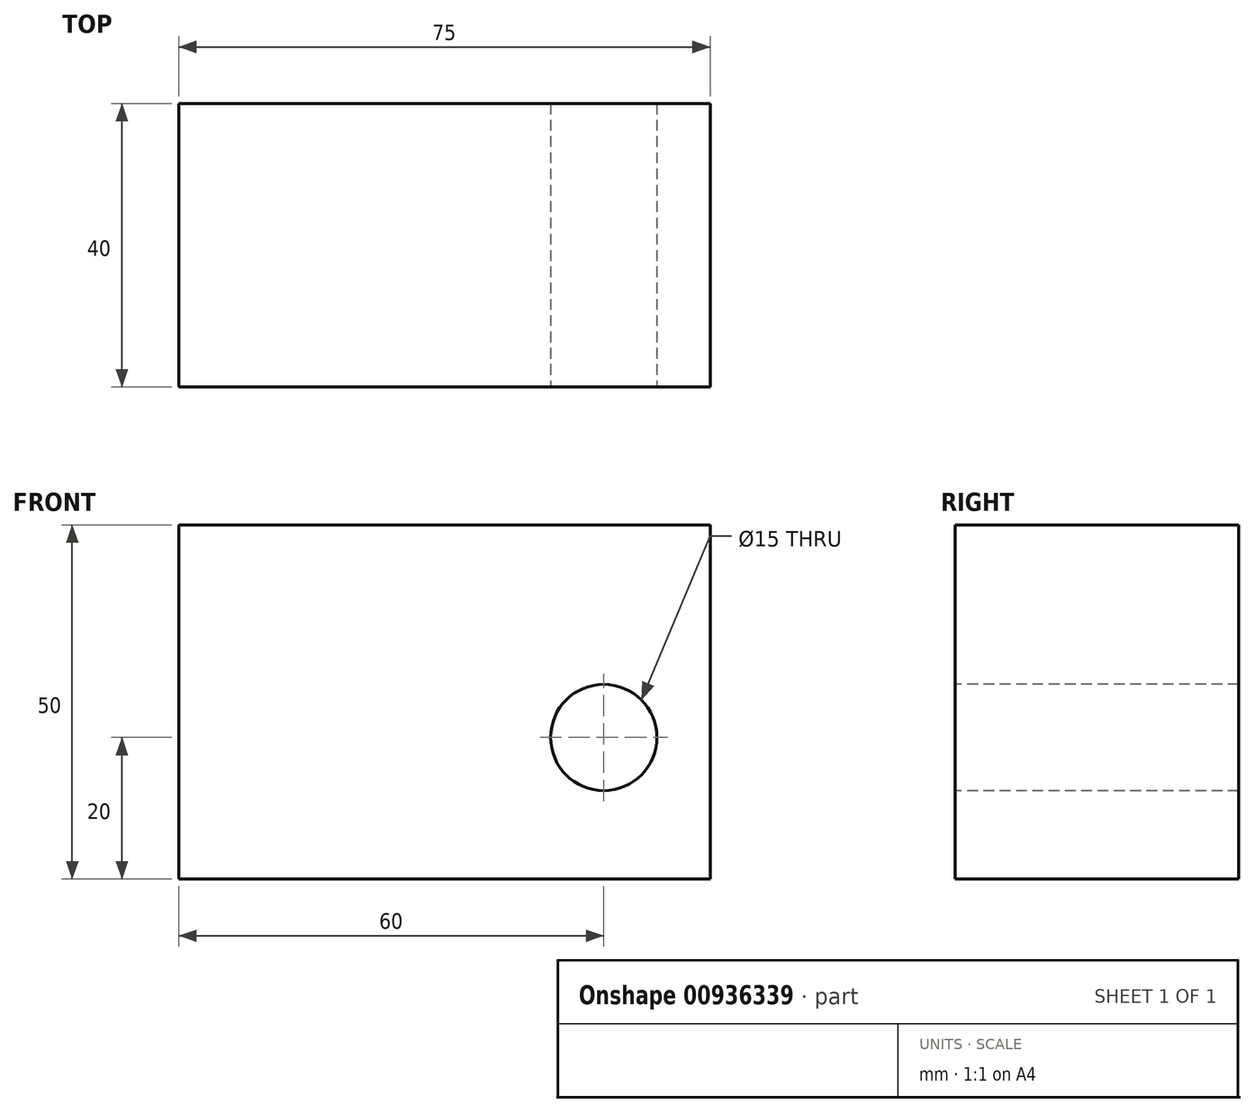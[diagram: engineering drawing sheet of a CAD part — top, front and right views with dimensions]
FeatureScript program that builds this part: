
annotation { "Feature Type Name" : "Feature", "Feature Type Description" : "" }
export const myFeature = defineFeature(function(context is Context, id is Id, definition is map)
    precondition{}
    {
        {
            var Q0;
            Q0=qCreatedBy(makeId("Front.planeOp"),FACE);
            var sketch = newSketch(context, id + "F0", { "sketchPlane" : qUnion([Q0])});
            skLineSegment(sketch, "E0.bottom", {"start": v(15, -20) * mm, "end": v(-60, -20) * mm});
            skLineSegment(sketch, "E0.top", {"start": v(15, 30) * mm, "end": v(-60, 30) * mm});
            skLineSegment(sketch, "E0.left", {"start": v(15, -20) * mm, "end": v(15, 30) * mm});
            skLineSegment(sketch, "E0.right", {"start": v(-60, -20) * mm, "end": v(-60, 30) * mm});
            skSolve(sketch);
        }
        {
            var Q0;
            Q0 = qSketchRegion(id + "F0", true);
            extrude(context, id + "F1", {"entities" : qUnion([Q0]), "depth" : 40 * mm, "offsetDistance" : 25 * mm, "symmetric" : true});
        }
        {
            var Q0;
            Q0=makeQuery(id+"F1.opExtrude","CAP_FACE",FACE,{"disambiguationData":[OSD([sQuery(id+"F0.wireOp",EDGE,"E0.bottom"),sQuery(id+"F0.wireOp",EDGE,"E0.top"),sQuery(id+"F0.wireOp",EDGE,"E0.left"),sQuery(id+"F0.wireOp",EDGE,"E0.right")])],"isStart":false});
            var sketch = newSketch(context, id + "F2", { "sketchPlane" : qUnion([Q0])});
            skCircle(sketch, "E1", {"center": v(0, 0) * mm, "radius": 7.5 * mm});
            skSolve(sketch);
        }
        {
            var Q0;
            Q0=makeQuery(id+"F2.imprint","IMPRINT",FACE,{"disambiguationData":[TD([[makeQuery(id+"F2.imprint","IMPRINT",EDGE,{"derivedFrom":sQuery(id+"F2.wireOp",EDGE,"E1")}),1.0]])]});
            var Q1;
            Q1=makeQuery(id+"F1.opExtrude","CAP_FACE",FACE,{"disambiguationData":[OSD([sQuery(id+"F0.wireOp",EDGE,"E0.bottom"),sQuery(id+"F0.wireOp",EDGE,"E0.top"),sQuery(id+"F0.wireOp",EDGE,"E0.left"),sQuery(id+"F0.wireOp",EDGE,"E0.right")])],"isStart":true});
            extrude(context, id + "F3", {"entities" : qUnion([Q0]), "operationType" : NewBodyOperationType.REMOVE, "endBound" : BoundingType.UP_TO_SURFACE, "oppositeDirection" : true, "depth" : -40 * mm, "endBoundEntityFace" : qUnion([Q1]), "offsetDistance" : 25 * mm});
        }
    });
